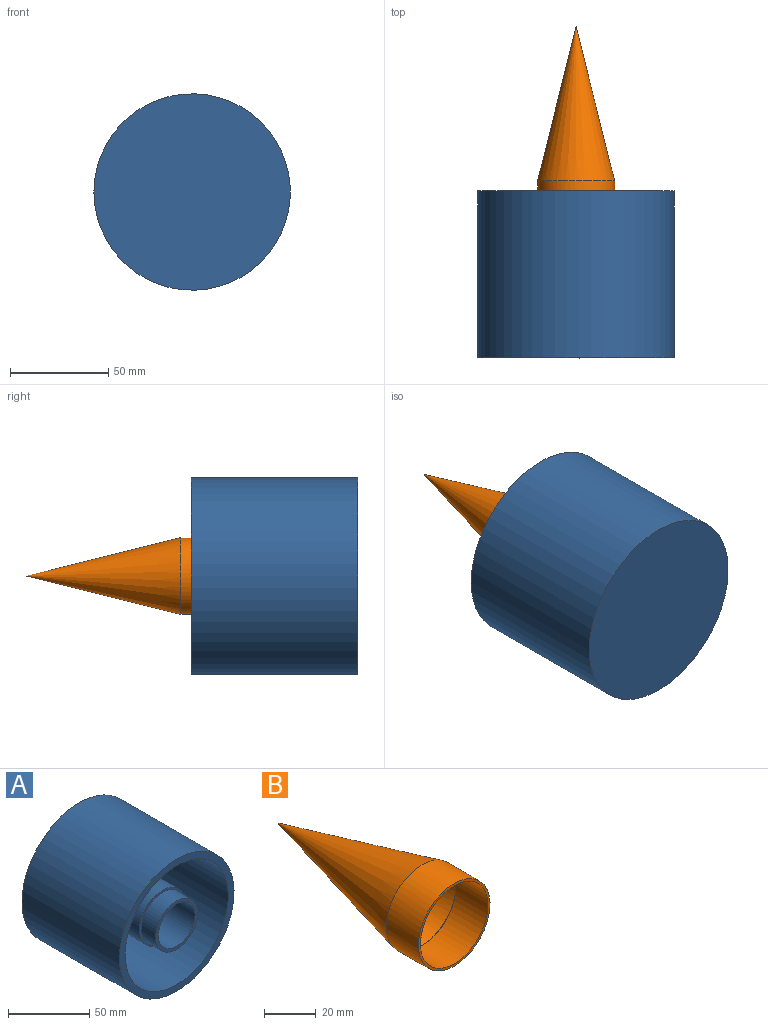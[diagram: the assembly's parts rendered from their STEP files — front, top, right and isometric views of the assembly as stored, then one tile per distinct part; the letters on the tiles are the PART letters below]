
ASSEMBLY  parts=2 mates=1
PART A: 11 faces, bbox 100x85x100 mm
  f0: cylinder r=20mm len=67.5mm, axis (0,1,0), area 8482.3mm2, adj f4,f6
  f1: cylinder r=45mm len=90mm, axis (0,1,0), area 22619.5mm2, adj f3,f4
  f2: cylinder r=50mm len=100mm, axis (0,1,0), area 26703.5mm2, adj f3,f5
  f3: plane 100x100mm, normal (0,-1,0), area 1492.3mm2, adj f1,f2
  f4: plane 90x90mm, normal (0,-1,0), area 5105.1mm2, adj f0,f1
  f5: plane 100x100mm, normal (0,1,0), area 7854mm2, adj f2
  f6: plane 40x40mm, normal (0,-1,0), area 200.9mm2, adj f0,f7
  f7: cylinder r=18.33mm len=36.66mm, axis (0,-1,0), area 1439.7mm2, adj f6,f10
  f8: plane 32x32mm, normal (0,-1,0), area 804.2mm2, adj f9
  f9: cylinder r=16mm len=80mm, axis (0,1,0), area 8042.5mm2, adj f8,f10
  f10: plane 36.66x36.66mm, normal (0,-1,0), area 251.4mm2, adj f7,f9
PART B: 6 faces, bbox 39.2x96.5x39.2 mm
  f0: cone r=0mm half-angle=14deg, axis (0,-1,0), area 5005.9mm2, adj f2
  f1: plane 37.14x37.14mm, normal (0,1,0), area 8.3mm2, adj f3,f5
  f2: cylinder r=19.6mm len=39.2mm, axis (0,1,0), area 2167.4mm2, adj f0,f4
  f3: cylinder r=18.5mm len=37mm, axis (0,1,0), area 2045.8mm2, adj f1,f4
  f4: plane 39.2x39.2mm, normal (0,-1,0), area 131.7mm2, adj f2,f3
  f5: cone r=0mm half-angle=14deg, axis (0,-1,0), area 4493.5mm2, adj f1
PLACE A rot(axis=(0.71,0,0.71),180deg) t=(-15.57,-229.52,-56.42)mm
PLACE B t=(-15.57,-144.42,-56.42)mm
MATE fastened B.f2 <-> A.f7  axis (0,-1,0) through (-15.57,-162.02,-56.42)mm
